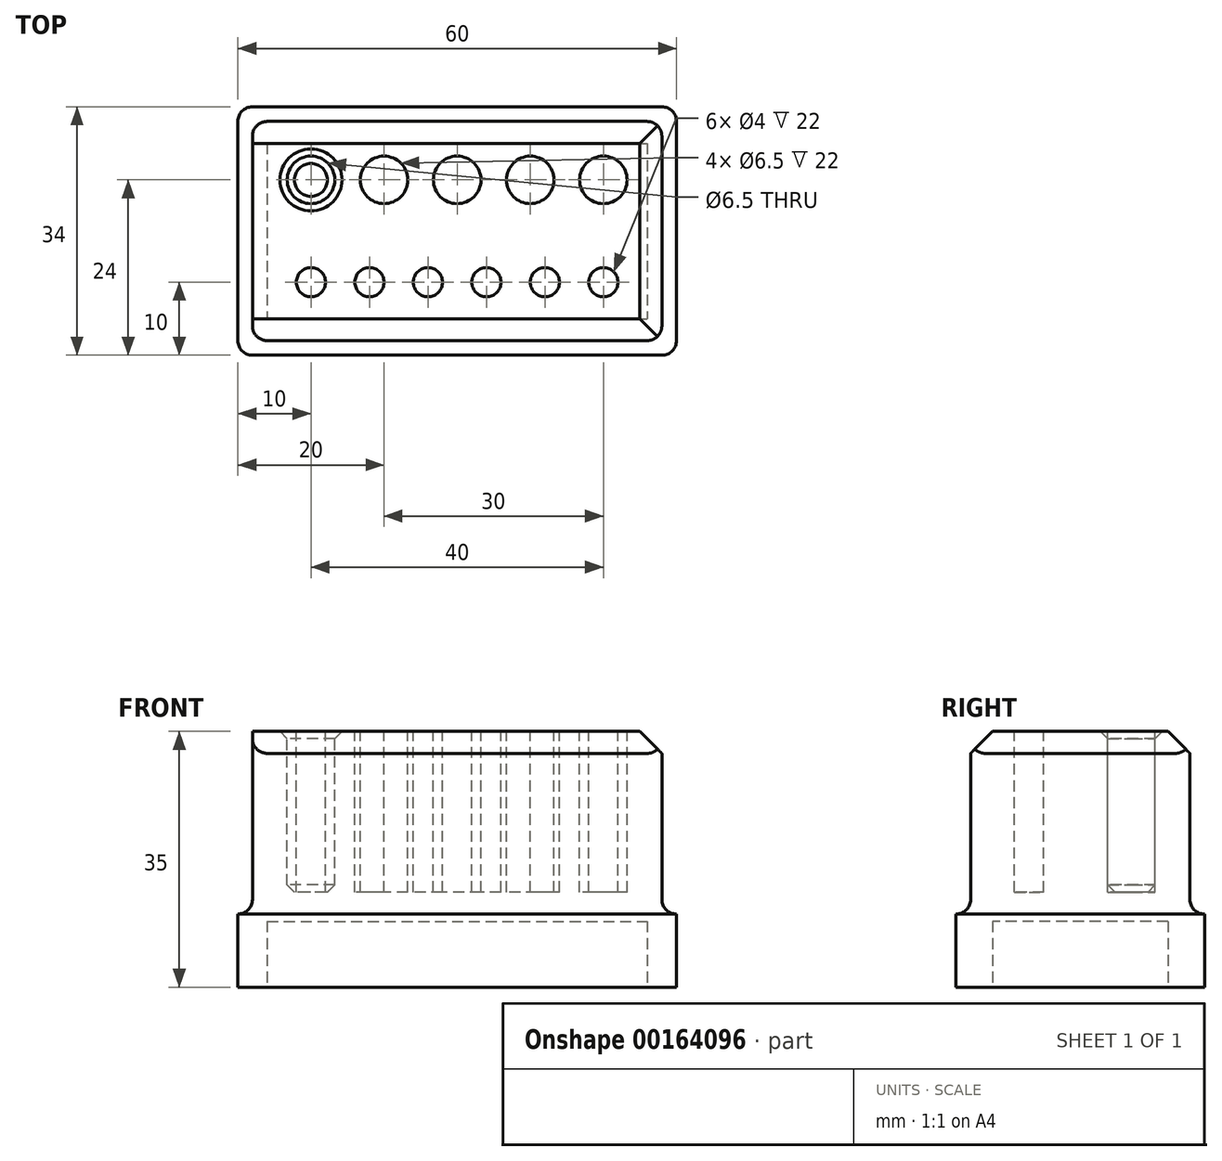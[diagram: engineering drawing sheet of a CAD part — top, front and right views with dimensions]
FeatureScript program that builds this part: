
annotation { "Feature Type Name" : "Feature", "Feature Type Description" : "" }
export const myFeature = defineFeature(function(context is Context, id is Id, definition is map)
    precondition{}
    {
        {
            var Q0;
            Q0=qCreatedBy(makeId("Top.planeOp"),FACE);
            var sketch = newSketch(context, id + "F0", { "sketchPlane" : qUnion([Q0])});
            skLineSegment(sketch, "E0.bottom", {"start": v(30, -17) * mm, "end": v(-30, -17) * mm});
            skLineSegment(sketch, "E0.top", {"start": v(30, 17) * mm, "end": v(-30, 17) * mm});
            skLineSegment(sketch, "E0.left", {"start": v(30, -17) * mm, "end": v(30, 17) * mm});
            skLineSegment(sketch, "E0.right", {"start": v(-30, -17) * mm, "end": v(-30, 17) * mm});
            skPoint(sketch, "E0.middle", {"position": v(0, 0) * mm});
            skLineSegment(sketch, "E1.0", {"start": v(28, 15) * mm, "end": v(-28, 15) * mm});
            skLineSegment(sketch, "E1.1", {"start": v(28, -15) * mm, "end": v(28, 15) * mm});
            skLineSegment(sketch, "E1.2", {"start": v(28, -15) * mm, "end": v(-28, -15) * mm});
            skLineSegment(sketch, "E1.3", {"start": v(-28, -15) * mm, "end": v(-28, 15) * mm});
            skSolve(sketch);
        }
        {
            var Q0;
            Q0=makeQuery(id+"F0.imprint","IMPRINT",FACE,{"disambiguationData":[TD([[makeQuery(id+"F0.imprint","IMPRINT",EDGE,{"derivedFrom":sQuery(id+"F0.wireOp",EDGE,"E1.0")}),1.0]])]});
            var Q1;
            Q1=makeQuery(id+"F0.imprint","IMPRINT",FACE,{"disambiguationData":[TD([[makeQuery(id+"F0.imprint","IMPRINT",EDGE,{"derivedFrom":sQuery(id+"F0.wireOp",EDGE,"E0.bottom")}),-1.0]])]});
            extrude(context, id + "F1", {"entities" : qUnion([Q0, Q1]), "depth" : 10 * mm});
        }
        {
            var Q0;
            Q0=makeQuery(id+"F0.imprint","IMPRINT",FACE,{"disambiguationData":[TD([[makeQuery(id+"F0.imprint","IMPRINT",EDGE,{"derivedFrom":sQuery(id+"F0.wireOp",EDGE,"E1.0")}),1.0]])]});
            extrude(context, id + "F2", {"entities" : qUnion([Q0]), "operationType" : NewBodyOperationType.ADD, "depth" : 35 * mm});
        }
        {
            var Q0;
            Q0=makeQuery(id+"F2.opExtrude","CAP_FACE",FACE,{"disambiguationData":[OSD([sQuery(id+"F0.wireOp",EDGE,"E1.0"),sQuery(id+"F0.wireOp",EDGE,"E1.1"),sQuery(id+"F0.wireOp",EDGE,"E1.2"),sQuery(id+"F0.wireOp",EDGE,"E1.3")])],"isStart":false});
            var sketch = newSketch(context, id + "F3", { "sketchPlane" : qUnion([Q0])});
            skCircle(sketch, "E2", {"center": v(-20, -7) * mm, "radius": 2 * mm});
            skCircle(sketch, "E3.1.0.0", {"center": v(-12, -7) * mm, "radius": 2 * mm});
            skCircle(sketch, "E3.2.0.0", {"center": v(-4, -7) * mm, "radius": 2 * mm});
            skCircle(sketch, "E3.3.0.0", {"center": v(4, -7) * mm, "radius": 2 * mm});
            skCircle(sketch, "E3.4.0.0", {"center": v(12, -7) * mm, "radius": 2 * mm});
            skCircle(sketch, "E3.5.0.0", {"center": v(20, -7) * mm, "radius": 2 * mm});
            skLineSegment(sketch, "E3.direction1", {"start": v(-20, -7) * mm, "end": v(-12, -7) * mm, "construction": true});
            skCircle(sketch, "E4", {"center": v(-20, 7) * mm, "radius": 3.25 * mm});
            skCircle(sketch, "E5.1.0.0", {"center": v(-10, 7) * mm, "radius": 3.25 * mm});
            skCircle(sketch, "E5.2.0.0", {"center": v(0, 7) * mm, "radius": 3.25 * mm});
            skCircle(sketch, "E5.3.0.0", {"center": v(10, 7) * mm, "radius": 3.25 * mm});
            skCircle(sketch, "E5.4.0.0", {"center": v(20, 7) * mm, "radius": 3.25 * mm});
            skLineSegment(sketch, "E5.direction1", {"start": v(-20, 7) * mm, "end": v(-10, 7) * mm, "construction": true});
            skSolve(sketch);
        }
        {
            var Q0;
            Q0 = qSketchRegion(id + "F3", true);
            extrude(context, id + "F4", {"entities" : qUnion([Q0]), "operationType" : NewBodyOperationType.REMOVE, "oppositeDirection" : true, "depth" : 22 * mm});
        }
        {
            var Q0;
            Q0=makeQuery(id+"F2.opExtrude","CAP_EDGE",EDGE,{"disambiguationData":[OSD([sQuery(id+"F0.wireOp",EDGE,"E1.0")])],"isStart":false});
            var Q1;
            Q1=makeQuery(id+"F2.opExtrude","CAP_EDGE",EDGE,{"disambiguationData":[OSD([sQuery(id+"F0.wireOp",EDGE,"E1.1")])],"isStart":false});
            var Q2;
            Q2=makeQuery(id+"F2.opExtrude","CAP_EDGE",EDGE,{"disambiguationData":[OSD([sQuery(id+"F0.wireOp",EDGE,"E1.2")])],"isStart":false});
            chamfer(context, id + "F5", {"entities" : qUnion([Q0, Q1, Q2]), "width" : 3 * mm, "tangentPropagation" : true});
        }
        {
            var Q0;
            Q0=makeQuery(id+"F4.boolean.opBoolean","COPY",FACE,{"derivedFrom":makeQuery(id+"F4.opExtrude","SWEPT_FACE",FACE,{"disambiguationData":[OSD([sQuery(id+"F3.wireOp",EDGE,"E4")])]})});
            var Q1;
            Q1=makeQuery(id+"F4.boolean.opBoolean","COPY",EDGE,{"derivedFrom":makeQuery(id+"F4.opExtrude","CAP_EDGE",EDGE,{"disambiguationData":[OSD([sQuery(id+"F3.wireOp",EDGE,"E5.1.0.0")])],"isStart":true})});
            var Q2;
            Q2=makeQuery(id+"F4.boolean.opBoolean","COPY",EDGE,{"derivedFrom":makeQuery(id+"F4.opExtrude","CAP_EDGE",EDGE,{"disambiguationData":[OSD([sQuery(id+"F3.wireOp",EDGE,"E5.2.0.0")])],"isStart":true})});
            var Q3;
            Q3=makeQuery(id+"F4.boolean.opBoolean","COPY",EDGE,{"derivedFrom":makeQuery(id+"F4.opExtrude","CAP_EDGE",EDGE,{"disambiguationData":[OSD([sQuery(id+"F3.wireOp",EDGE,"E5.3.0.0")])],"isStart":true})});
            var Q4;
            Q4=makeQuery(id+"F4.boolean.opBoolean","COPY",EDGE,{"derivedFrom":makeQuery(id+"F4.opExtrude","CAP_EDGE",EDGE,{"disambiguationData":[OSD([sQuery(id+"F3.wireOp",EDGE,"E5.4.0.0")])],"isStart":true})});
            var Q5;
            Q5=makeQuery(id+"F4.boolean.opBoolean","COPY",EDGE,{"derivedFrom":makeQuery(id+"F4.opExtrude","CAP_EDGE",EDGE,{"disambiguationData":[OSD([sQuery(id+"F3.wireOp",EDGE,"E2")])],"isStart":true})});
            var Q6;
            Q6=makeQuery(id+"F4.boolean.opBoolean","COPY",EDGE,{"derivedFrom":makeQuery(id+"F4.opExtrude","CAP_EDGE",EDGE,{"disambiguationData":[OSD([sQuery(id+"F3.wireOp",EDGE,"E3.1.0.0")])],"isStart":true})});
            var Q7;
            Q7=makeQuery(id+"F4.boolean.opBoolean","COPY",EDGE,{"derivedFrom":makeQuery(id+"F4.opExtrude","CAP_EDGE",EDGE,{"disambiguationData":[OSD([sQuery(id+"F3.wireOp",EDGE,"E3.2.0.0")])],"isStart":true})});
            var Q8;
            Q8=makeQuery(id+"F4.boolean.opBoolean","COPY",EDGE,{"derivedFrom":makeQuery(id+"F4.opExtrude","CAP_EDGE",EDGE,{"disambiguationData":[OSD([sQuery(id+"F3.wireOp",EDGE,"E3.3.0.0")])],"isStart":true})});
            var Q9;
            Q9=makeQuery(id+"F4.boolean.opBoolean","COPY",EDGE,{"derivedFrom":makeQuery(id+"F4.opExtrude","CAP_EDGE",EDGE,{"disambiguationData":[OSD([sQuery(id+"F3.wireOp",EDGE,"E3.4.0.0")])],"isStart":true})});
            var Q10;
            Q10=makeQuery(id+"F4.boolean.opBoolean","COPY",EDGE,{"derivedFrom":makeQuery(id+"F4.opExtrude","CAP_EDGE",EDGE,{"disambiguationData":[OSD([sQuery(id+"F3.wireOp",EDGE,"E3.5.0.0")])],"isStart":true})});
            chamfer(context, id + "F6", {"entities" : qUnion([Q0, Q1, Q2, Q3, Q4, Q5, Q6, Q7, Q8, Q9, Q10]), "width" : 1 * mm, "tangentPropagation" : true});
        }
        {
            var Q0;
            Q0=makeQuery(id+"F2.opExtrude","SWEPT_EDGE",EDGE,{"disambiguationData":[OSD([sQuery(id+"F0.wireOp",EDGE,"E1.1"),sQuery(id+"F0.wireOp",EDGE,"E1.2")])]});
            var Q1;
            Q1=makeQuery(id+"F2.opExtrude","SWEPT_EDGE",EDGE,{"disambiguationData":[OSD([sQuery(id+"F0.wireOp",EDGE,"E1.2"),sQuery(id+"F0.wireOp",EDGE,"E1.3")])]});
            var Q2;
            Q2=makeQuery(id+"F2.opExtrude","SWEPT_EDGE",EDGE,{"disambiguationData":[OSD([sQuery(id+"F0.wireOp",EDGE,"E1.0"),sQuery(id+"F0.wireOp",EDGE,"E1.1")])]});
            var Q3;
            Q3=makeQuery(id+"F2.opExtrude","SWEPT_EDGE",EDGE,{"disambiguationData":[OSD([sQuery(id+"F0.wireOp",EDGE,"E1.0"),sQuery(id+"F0.wireOp",EDGE,"E1.3")])]});
            fillet(context, id + "F7", {"entities" : qUnion([Q0, Q1, Q2, Q3]), "radius" : 2 * mm, "tangentPropagation" : true, "allowEdgeOverflow" : false});
        }
        {
            var Q0;
            Q0=makeQuery(id+"F1.opExtrude","SWEPT_EDGE",EDGE,{"disambiguationData":[OSD([sQuery(id+"F0.wireOp",EDGE,"E0.bottom"),sQuery(id+"F0.wireOp",EDGE,"E0.right")])]});
            var Q1;
            Q1=makeQuery(id+"F2.boolean.opBoolean","INTERSECT",EDGE,{"derivedFrom":[makeQuery(id+"F1.opExtrude","CAP_FACE",FACE,{"disambiguationData":[OSD([sQuery(id+"F0.wireOp",EDGE,"E0.bottom"),sQuery(id+"F0.wireOp",EDGE,"E0.top"),sQuery(id+"F0.wireOp",EDGE,"E0.left"),sQuery(id+"F0.wireOp",EDGE,"E0.right")])],"isStart":false}),makeQuery(id+"F2.opExtrude","SWEPT_FACE",FACE,{"disambiguationData":[OSD([sQuery(id+"F0.wireOp",EDGE,"E1.2")])]})]});
            var Q2;
            Q2=makeQuery(id+"F1.opExtrude","SWEPT_EDGE",EDGE,{"disambiguationData":[OSD([sQuery(id+"F0.wireOp",EDGE,"E0.bottom"),sQuery(id+"F0.wireOp",EDGE,"E0.left")])]});
            var Q3;
            Q3=makeQuery(id+"F1.opExtrude","SWEPT_EDGE",EDGE,{"disambiguationData":[OSD([sQuery(id+"F0.wireOp",EDGE,"E0.top"),sQuery(id+"F0.wireOp",EDGE,"E0.left")])]});
            var Q4;
            Q4=makeQuery(id+"F1.opExtrude","SWEPT_EDGE",EDGE,{"disambiguationData":[OSD([sQuery(id+"F0.wireOp",EDGE,"E0.top"),sQuery(id+"F0.wireOp",EDGE,"E0.right")])]});
            fillet(context, id + "F8", {"entities" : qUnion([Q0, Q1, Q2, Q3, Q4]), "radius" : 2 * mm, "tangentPropagation" : true, "allowEdgeOverflow" : false});
        }
        {
            var Q0;
            Q0=makeQuery(id+"F0.imprint","IMPRINT",FACE,{"disambiguationData":[TD([[makeQuery(id+"F0.imprint","IMPRINT",EDGE,{"derivedFrom":sQuery(id+"F0.wireOp",EDGE,"E1.0")}),1.0]])]});
            var sketch = newSketch(context, id + "F9", { "sketchPlane" : qUnion([Q0])});
            skLineSegment(sketch, "E6.bottom", {"start": v(-26, 12) * mm, "end": v(26, 12) * mm});
            skLineSegment(sketch, "E6.top", {"start": v(-26, -12) * mm, "end": v(26, -12) * mm});
            skLineSegment(sketch, "E6.left", {"start": v(-26, 12) * mm, "end": v(-26, -12) * mm});
            skLineSegment(sketch, "E6.right", {"start": v(26, 12) * mm, "end": v(26, -12) * mm});
            skPoint(sketch, "E6.middle", {"position": v(0, 0) * mm});
            skSolve(sketch);
        }
        {
            var Q0;
            Q0=makeQuery(id+"F9.imprint","IMPRINT",FACE,{"disambiguationData":[TD([[makeQuery(id+"F9.imprint","IMPRINT",EDGE,{"derivedFrom":sQuery(id+"F9.wireOp",EDGE,"E6.bottom")}),-1.0]])]});
            var Q1;
            Q1=sQuery(id+"F9.wireOp",EDGE,"E6.left");
            var Q2;
            Q2=sQuery(id+"F9.wireOp",EDGE,"E6.top");
            var Q3;
            Q3=sQuery(id+"F9.wireOp",EDGE,"E6.right");
            var Q4;
            Q4=sQuery(id+"F9.wireOp",EDGE,"E6.bottom");
            extrude(context, id + "F10", {"entities" : qUnion([Q0]), "surfaceEntities" : qUnion([Q1, Q2, Q3, Q4]), "depth" : 9 * mm});
        }
    });
